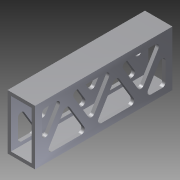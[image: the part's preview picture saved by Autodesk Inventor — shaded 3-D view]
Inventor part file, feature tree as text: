
AUTODESK INVENTOR PART (.ipt)
format: ipt  version: 2012 (Build 160160000, 160)  size: 247,808 bytes
history: native  units: in
note: dims shown in document units (in); Inventor stores cm internally (conversion verified against a paired STEP export)
features: extrude x3, sketch x3, fillet x1
ambient origin geometry x8: Origin, YZ Plane, XZ Plane, XY Plane, X Axis, Y Axis, Z Axis, Center Point
bodies: Solid1 (feature_tree)
feature tree (7):
  extrude  "Extrusion1"  Depth=1.0in
  extrude  "Extrusion5"  Depth=0.125in
  extrude  "Extrusion6"  Depth=0.125in
  fillet  "Fillet1"  Radius=5.0in
  sketch  "Sketch1"  dims[d0=2.0in d1=1.0in]
  sketch  "Sketch4"  dims[d2=0.125in d3=0.125in]
  sketch  "Sketch5"  dims[d4=0.125in d5=0.125in d6=5.0in d7=0.0in d20=0.2128in d21=0.4255in d22=0.4255in d23=0.4255in d24=0.4255in d25=0.125in d26=0.125in d27=0.125in d28=0.125in d29=0.125in d30=0.125in d31=0.125in d32=0.125in d33=0.125in d34=0.125in d35=0.25in d36=0.25in d37=0.25in d38=0.25in d39=0.125in d40=0.0in d41=0.2128in d42=0.4255in d43=0.4255in d44=0.4255in d45=0.4255in d46=0.125in d47=0.125in d48=0.125in d49=0.125in d50=0.125in d51=0.125in d52=0.125in d53=0.125in d54=0.125in d55=0.125in d56=0.25in d57=0.25in d58=0.25in d59=0.25in d60=0.125in d61=0.0in d62=0.125in]
